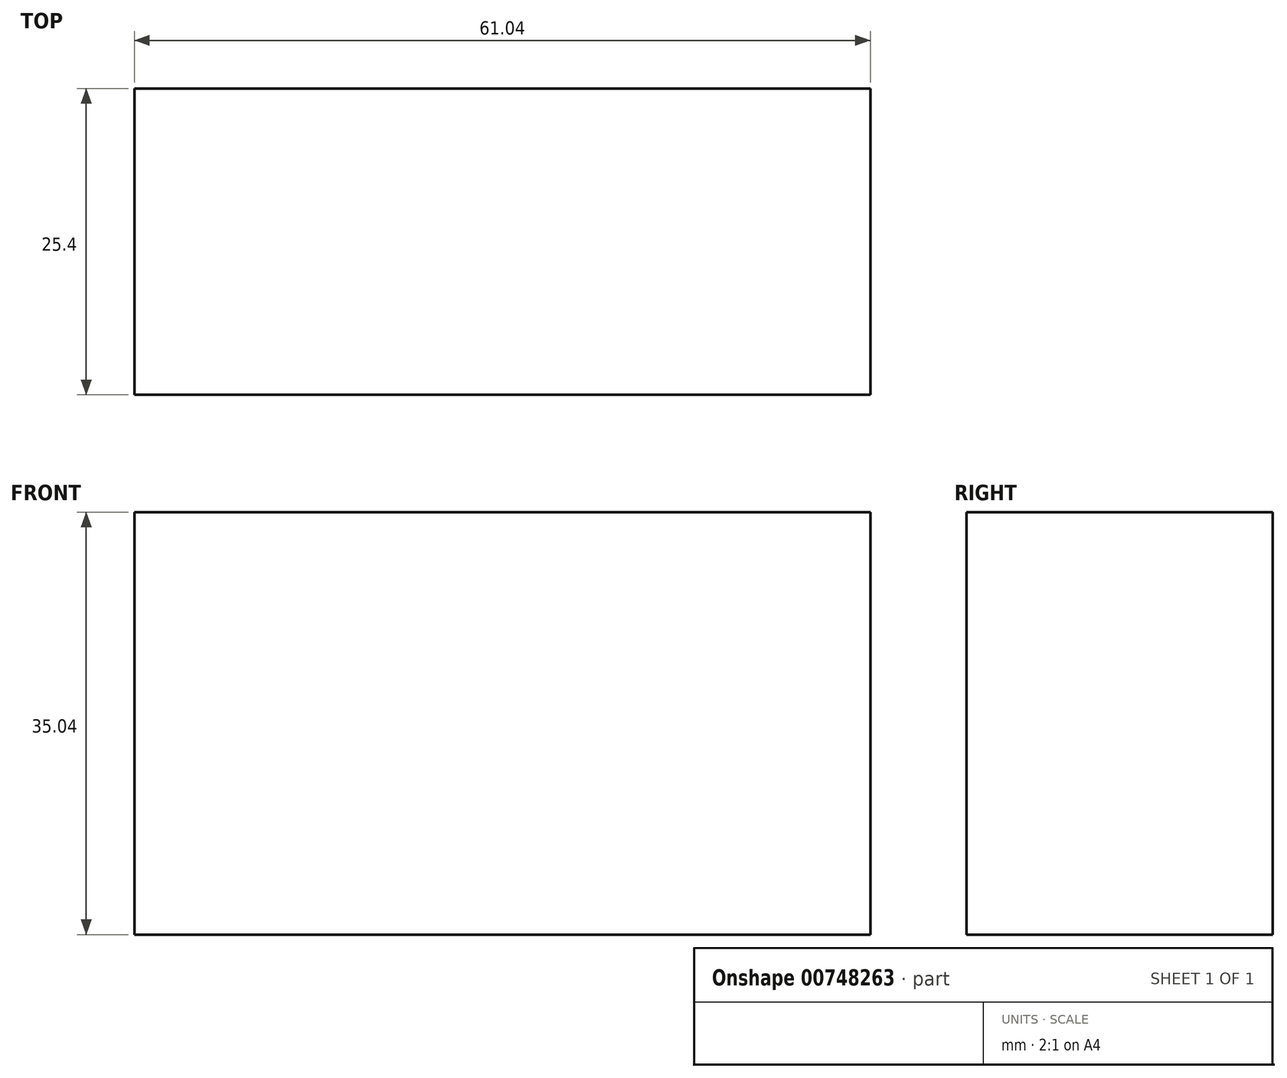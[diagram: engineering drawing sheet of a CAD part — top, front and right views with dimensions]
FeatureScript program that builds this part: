
annotation { "Feature Type Name" : "Feature", "Feature Type Description" : "" }
export const myFeature = defineFeature(function(context is Context, id is Id, definition is map)
    precondition{}
    {
        {
            var Q0;
            Q0=qCreatedBy(makeId("Front.planeOp"),FACE);
            var sketch = newSketch(context, id + "F0", { "sketchPlane" : qUnion([Q0])});
            skLineSegment(sketch, "E0.bottom", {"start": v(-61.04, 35.04) * mm, "end": v(0, 35.04) * mm});
            skLineSegment(sketch, "E0.top", {"start": v(-61.04, 0) * mm, "end": v(0, 0) * mm});
            skLineSegment(sketch, "E0.left", {"start": v(-61.04, 35.04) * mm, "end": v(-61.04, 0) * mm});
            skLineSegment(sketch, "E0.right", {"start": v(0, 35.04) * mm, "end": v(0, 0) * mm});
            skSolve(sketch);
        }
        {
            var Q0;
            Q0=makeQuery(id+"F0.imprint","IMPRINT",FACE,{"disambiguationData":[TD([[makeQuery(id+"F0.imprint","IMPRINT",EDGE,{"derivedFrom":sQuery(id+"F0.wireOp",EDGE,"E0.bottom")}),-1.0]])]});
            extrude(context, id + "F1", {"entities" : qUnion([Q0]), "depth" : 25.4 * mm, "offsetDistance" : 25.4 * mm});
        }
    });
